# Revit family: Astro Mast Twin Concrete
name_source: partatom
category: Lighting Fixtures
revit_build: Autodesk Revit 2018 (Build: 20170223_1515(x64)
units: mm (PartAtom-declared; Revit-internal decimal feet)

## family parameters
Always vertical = Yes
Cut with Voids When Loaded = No
Host = Wall
Light Source = No
OmniClass Number = 23.80.70.00
OmniClass Title = Lighting
Part Type = Normal
Room Calculation Point = No
Round Connector Dimension = Use Diameter
Shared = No

## types (1)
- Astro - Mast Twin
    ADA compliant = N / A
    Dimmable = Lamp Dependent
    Dimming Method = Lamp Dependent
    Driver Required = No
    Efficacy (lm/w) = Lamp Dependent
    Electrical Class = 1
    Lamp = 2 X GU 10 LED
    Length of Cable Supplied = -
    Light Source Fixed = No
    Location / IP Rating = IP44
    Main Finish = Matt Concrete
    Main Material = Concrete and Metal - Brass
    Manufacturer = Astro Lighting Ltd
    Manufacturer URL - Europe and Rest of World = www.astrolighting.com
    Manufacturer URL - North America = us.astrolighting.com
    Power (Watts) = 2 x 6 Watt Max
    Product CCT = Lamp Dependent
    Product CRI = Lamp Dependent
    Product Dimensions (MM) = H 138 W 230 D 88
    Product Location = Outdoor/Coastal/Indoor/Bathroom
    Product Name = Mast Twin
    Product SKU = 1317013
    Product URL = https://www.astrolighting.com
    Product Weight (KG) = 1.5
    URL = www.astrolighting.com
    Wattage Comments = -

## geometry (parser evidence)
native form markers: Sweep x2
no freeform markers — native parametric forms only
